# Revit family: ledflood-p_re440-125w-4000-w-bl_140062032
name_source: partatom
category: Lighting Fixtures
units: mm (PartAtom-declared; Revit-internal decimal feet)

## family parameters
Cut with Voids When Loaded = No
Host = Face
Light Source = No
Part Type = Normal
Room Calculation Point = No
Round Connector Dimension = Use Diameter
Shared = No

## types (1)
- LEDFlood-P Re440-125W-4000-W-BL (1 x LED, 15625 lm, 4000)
    Apparent Load = 125 VA
    Approval mark = CE, ENEC
    CIE Flux Codes = 60 92 99 100 100
    Color Rendering = 80
    Color Temperature = 4000
    Control Gear = Electronic ballast
    Default Elevation = 1800 mm
    Description = Precise optical design for area-, object- and façade lighting. Super slim aluminium body with integrated heatsink and clipless cover. Improved 100,000 hour (L70) lifetime. Robust design with high protection against water and dust. Equipped with a valve to
    Height = 65 mm
    Lamp = 1 x LED
    Lamp Light Flux = 15625 lm
    Lamp count = 1
    Length = 440 mm
    Luminous efficacy = 125 lm/W
    Manufacturer = OPPLE
    ModVariant = No
    Model = 140062032
    Mounting Place = Wall
    Mounting Type = Surface mounted
    Number of Poles = 1
    OnlyDefault = Yes
    Power Factor = 1
    Product Name = LEDFlood-P Re440-125W-4000-W-BL
    Product group = Floodlight Performer
    ProductGroupID = 2005
    Protection Class = Protection class I
    Protection Degree = IP 66
    RLX_Detail_Level = 1
    RlxData = <blob elided: 47381 chars, md5=7f856c88>
    Socket = socket
    Standby Power = 0 W
    System Light Flux = 15624 lm
    System Power = 125 W
    Type Comments = Product without accessories
    Type Image = 140062032.jpg
    URL = http://relux.com
    VarID = ---
    Voltage = 0 V
    Weight = 0.00 kg
    Width = 330 mm

## geometry (parser evidence)
native form markers: Sweep x10
no freeform markers — native parametric forms only
